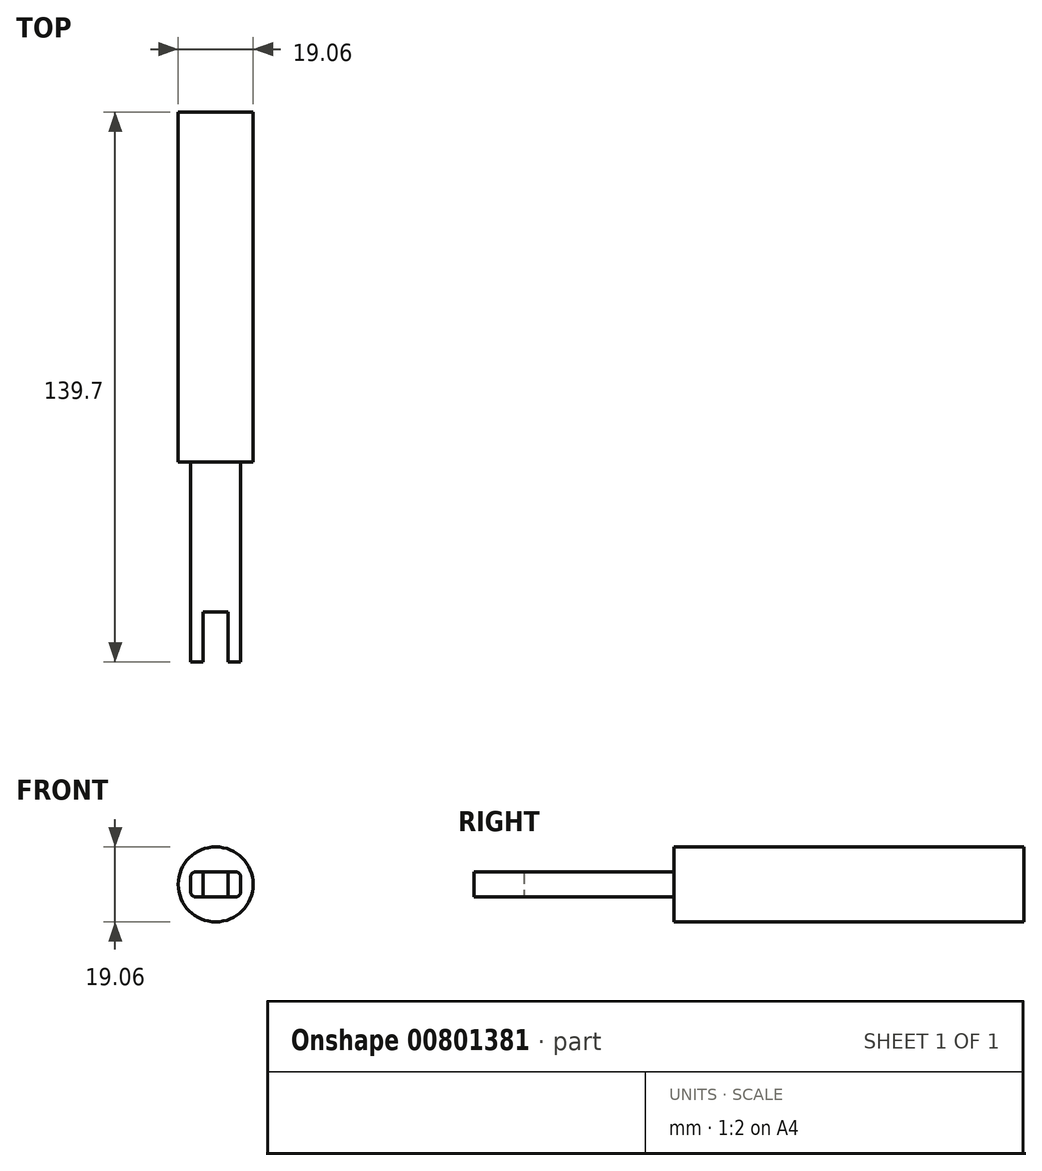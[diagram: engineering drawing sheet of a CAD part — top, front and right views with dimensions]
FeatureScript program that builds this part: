
annotation { "Feature Type Name" : "Feature", "Feature Type Description" : "" }
export const myFeature = defineFeature(function(context is Context, id is Id, definition is map)
    precondition{}
    {
        {
            var Q0;
            Q0=qCreatedBy(makeId("Front.planeOp"),FACE);
            var sketch = newSketch(context, id + "F0", { "sketchPlane" : qUnion([Q0])});
            skCircle(sketch, "E0", {"center": v(0, 0) * mm, "radius": 9.53 * mm});
            skSolve(sketch);
        }
        {
            var Q0;
            Q0=makeQuery(id+"F0.imprint","IMPRINT",FACE,{"disambiguationData":[TD([[makeQuery(id+"F0.imprint","IMPRINT",EDGE,{"derivedFrom":sQuery(id+"F0.wireOp",EDGE,"E0")}),1.0]])]});
            extrude(context, id + "F1", {"entities" : qUnion([Q0]), "oppositeDirection" : true, "depth" : 88.9 * mm, "offsetDistance" : 25.4 * mm});
        }
        {
            var Q0;
            Q0=makeQuery(id+"F1.opExtrude","CAP_FACE",FACE,{"disambiguationData":[OSD([sQuery(id+"F0.wireOp",EDGE,"E0")])],"isStart":true});
            var sketch = newSketch(context, id + "F2", { "sketchPlane" : qUnion([Q0])});
            skLineSegment(sketch, "E1.bottom", {"start": v(6.35, 3.18) * mm, "end": v(-6.35, 3.18) * mm});
            skLineSegment(sketch, "E1.top", {"start": v(6.35, -3.18) * mm, "end": v(-6.35, -3.18) * mm});
            skLineSegment(sketch, "E1.left", {"start": v(6.35, 3.18) * mm, "end": v(6.35, -3.18) * mm});
            skLineSegment(sketch, "E1.right", {"start": v(-6.35, 3.18) * mm, "end": v(-6.35, -3.18) * mm});
            skPoint(sketch, "E1.middle", {"position": v(0, 0) * mm});
            skSolve(sketch);
        }
        {
            var Q0;
            Q0=makeQuery(id+"F2.imprint","IMPRINT",FACE,{"disambiguationData":[TD([[makeQuery(id+"F2.imprint","IMPRINT",EDGE,{"derivedFrom":sQuery(id+"F2.wireOp",EDGE,"E1.bottom")}),1.0]])]});
            extrude(context, id + "F3", {"entities" : qUnion([Q0]), "operationType" : NewBodyOperationType.ADD, "depth" : 50.8 * mm, "offsetDistance" : 25.4 * mm});
        }
        {
            var Q0;
            Q0=makeQuery(id+"F3.opExtrude","CAP_FACE",FACE,{"disambiguationData":[OSD([sQuery(id+"F2.wireOp",EDGE,"E1.bottom"),sQuery(id+"F2.wireOp",EDGE,"E1.top"),sQuery(id+"F2.wireOp",EDGE,"E1.left"),sQuery(id+"F2.wireOp",EDGE,"E1.right")])],"isStart":false});
            var sketch = newSketch(context, id + "F4", { "sketchPlane" : qUnion([Q0])});
            skLineSegment(sketch, "E2.bottom", {"start": v(3.18, 3.18) * mm, "end": v(-3.18, 3.18) * mm});
            skLineSegment(sketch, "E2.top", {"start": v(3.18, -3.18) * mm, "end": v(-3.18, -3.18) * mm});
            skLineSegment(sketch, "E2.left", {"start": v(3.18, 3.18) * mm, "end": v(3.18, -3.18) * mm});
            skLineSegment(sketch, "E2.right", {"start": v(-3.18, 3.18) * mm, "end": v(-3.18, -3.18) * mm});
            skPoint(sketch, "E2.middle", {"position": v(0, 0) * mm});
            skSolve(sketch);
        }
        {
            var Q0;
            Q0=makeQuery(id+"F4.imprint","IMPRINT",FACE,{"disambiguationData":[TD([[makeQuery(id+"F4.imprint","IMPRINT",EDGE,{"derivedFrom":sQuery(id+"F4.wireOp",EDGE,"E2.bottom")}),1.0]])]});
            extrude(context, id + "F5", {"entities" : qUnion([Q0]), "operationType" : NewBodyOperationType.REMOVE, "oppositeDirection" : true, "depth" : 12.7 * mm, "offsetDistance" : 25.4 * mm});
        }
        {
            var Q0;
            Q0=makeQuery(id+"F3.opExtrude","SWEPT_EDGE",EDGE,{"disambiguationData":[OSD([sQuery(id+"F2.wireOp",EDGE,"E1.bottom"),sQuery(id+"F2.wireOp",EDGE,"E1.left")])]});
            var Q1;
            Q1=makeQuery(id+"F3.opExtrude","SWEPT_EDGE",EDGE,{"disambiguationData":[OSD([sQuery(id+"F2.wireOp",EDGE,"E1.bottom"),sQuery(id+"F2.wireOp",EDGE,"E1.right")])]});
            var Q2;
            Q2=makeQuery(id+"F3.opExtrude","SWEPT_EDGE",EDGE,{"disambiguationData":[OSD([sQuery(id+"F2.wireOp",EDGE,"E1.top"),sQuery(id+"F2.wireOp",EDGE,"E1.right")])]});
            var Q3;
            Q3=makeQuery(id+"F3.opExtrude","SWEPT_EDGE",EDGE,{"disambiguationData":[OSD([sQuery(id+"F2.wireOp",EDGE,"E1.top"),sQuery(id+"F2.wireOp",EDGE,"E1.left")])]});
            fillet(context, id + "F6", {"entities" : qUnion([Q0, Q1, Q2, Q3]), "radius" : 1.27 * mm, "tangentPropagation" : true, "allowEdgeOverflow" : false});
        }
    });
